# Revit family: GC-200-2000
name_source: partatom
category: Mechanical Equipment
units: mm (PartAtom-declared; Revit-internal decimal feet)

## family parameters
Always vertical = Yes
Cut with Voids When Loaded = No
Part Type = Normal
Room Calculation Point = No
Round Connector Dimension = Use Diameter
Shared = No
Work Plane-Based = No

## types (30) — shared parameters
0 = 0"
1" = 1"
1.5 = 1 1/2"
2" = 2"
2' = 24"
3" = 3"
4" = 4"
Manufacturer = Loren Cook Company
ONE EIGTH = 1/8"
Type Comments = Ceiling and Wall Blower 200-2000 Series
URL = www.lorencook.com

## per-type parameters (varying)
| type | (H/2)-(K/2) | A | A/2 | B | B/2 | H | H/2 | J | J/2 | K | K/2 | L | L/2 | Model | W | W/2 |
| GC-222/242_STEEL | -1 15/16" | 8" | 4" | 6" | 3" | 9 3/4" | 4 7/8" | 16 3/8" | 8 3/16" | 13 5/8" | 6 13/16" | 12 3/8" | 6 3/16" | GC | 9 3/4" | 4 7/8" |
| GC-322/342_STEEL | -1 7/16" | 8" | 4" | 6" | 3" | 10 3/4" | 5 3/8" | 16 3/8" | 8 3/16" | 13 5/8" | 6 13/16" | 12 3/8" | 6 3/16" | GC | 10 3/4" | 5 3/8" |
| GC-422_STEEL | -1 3/16" | 8" | 4" | 6" | 3" | 11 7/8" | 5 15/16" | 21" | 10 1/2" | 14 1/4" | 7 1/8" | 17" | 8 1/2" | GC | 11 7/8" | 5 15/16" |
| GC-520_STEEL | -1 3/16" | 8" | 4" | 6" | 3" | 11 7/8" | 5 15/16" | 21" | 10 1/2" | 14 1/4" | 7 1/8" | 17" | 8 1/2" | GC | 11 7/8" | 5 15/16" |
| GC-620/640_STEEL | -1 3/16" | 10 1/2" | 5 1/4" | 4 3/4" | 2 3/8" | 11 7/8" | 5 15/16" | 21" | 10 1/2" | 14 1/4" | 7 1/8" | 17" | 8 1/2" | GC | 11 7/8" | 5 15/16" |
| GC-720/740_STEEL | -1 3/16" | 10 1/2" | 5 1/4" | 4 3/4" | 2 3/8" | 11 7/8" | 5 15/16" | 21" | 10 1/2" | 14 1/4" | 7 1/8" | 17" | 8 1/2" | GC | 11 7/8" | 5 15/16" |
| GC-822/842/862_STEEL | -1 7/32" | 20" | 10" | 6" | 3" | 14 11/16" | 7 11/32" | 31 3/8" | 15 11/16" | 17 1/8" | 8 9/16" | 27" | 13 1/2" | GC | 14 11/16" | 7 11/32" |
| GC-920/940/960_STEEL | -1 7/32" | 24 1/4" | 12 1/8" | 6" | 3" | 14 11/16" | 7 11/32" | 35 1/8" | 17 9/16" | 17 1/8" | 8 9/16" | 31" | 15 1/2" | GC | 14 11/16" | 7 11/32" |
| GC-222/242_ALUMINUM | -3/4" | 8" | 4" | 6" | 3" | 9 3/4" | 4 7/8" | 14 1/4" | 7 1/8" | 11 1/4" | 5 5/8" | 12 3/8" | 6 3/16" | GC | 9 3/4" | 4 7/8" |
| GC-322/342_ALUMINUM | -3/4" | 8" | 4" | 6" | 3" | 10 3/4" | 5 3/8" | 14 1/4" | 7 1/8" | 12 1/4" | 6 1/8" | 12 3/8" | 6 3/16" | GC | 10 3/4" | 5 3/8" |
| GC-422_ALUMINUM | -15/16" | 8" | 4" | 6" | 3" | 11 7/8" | 5 15/16" | 18 3/4" | 9 3/8" | 13 3/4" | 6 7/8" | 17" | 8 1/2" | GC | 11 7/8" | 5 15/16" |
| GC-522/524_ALUMINUM | -15/16" | 8" | 4" | 6" | 3" | 11 7/8" | 5 15/16" | 18 3/4" | 9 3/8" | 13 3/4" | 6 7/8" | 17" | 8 1/2" | GC | 11 7/8" | 5 15/16" |
| GC-622/642_ALUMINUM | -15/16" | 10 1/2" | 5 1/4" | 4 3/4" | 2 3/8" | 11 7/8" | 5 15/16" | 18 3/4" | 9 3/8" | 13 3/4" | 6 7/8" | 17" | 8 1/2" | GC | 11 7/8" | 5 15/16" |
| GC-720/740_ALUMINUM | -15/16" | 10 1/2" | 5 1/4" | 4 3/4" | 2 3/8" | 11 7/8" | 5 15/16" | 18 3/4" | 9 3/8" | 13 3/4" | 6 7/8" | 17" | 8 1/2" | GC | 11 7/8" | 5 15/16" |
| GC-222/242_PLASTIC | -1 3/4" | 8" | 4" | 6" | 3" | 9 3/4" | 4 7/8" | 14 3/4" | 7 3/8" | 13 1/4" | 6 5/8" | 12 3/8" | 6 3/16" | GC | 9 3/4" | 4 7/8" |
| GC-822/842/862_ALUMINUM | -25/32" | 20" | 10" | 6" | 3" | 14 11/16" | 7 11/32" | 28 3/4" | 14 3/8" | 16 1/4" | 8 1/8" | 27" | 13 1/2" | GC | 14 11/16" | 7 11/32" |
| GC-920/940/960_ALUMINUM | -9/32" | 24 1/4" | 12 1/8" | 6" | 3" | 14 11/16" | 7 11/32" | 31 3/4" | 15 7/8" | 15 1/4" | 7 5/8" | 31" | 15 1/2" | GC | 14 11/16" | 7 11/32" |
| GC-1000_ALUMINUM | -1/4" | 33 11/16" | 16 27/32" | 7 11/16" | 3 27/32" | 15 1/4" | 7 5/8" | 38 3/4" | 19 3/8" | 15 3/4" | 7 7/8" | 38 1/8" | 19 1/16" | GC | 15 1/4" | 7 5/8" |
| GC-1000_STEEL | -15/16" | 33 11/16" | 16 27/32" | 7 11/16" | 3 27/32" | 15 1/4" | 7 5/8" | 42 3/8" | 21 3/16" | 17 1/8" | 8 9/16" | 38 1/8" | 19 1/16" | GC | 15 1/4" | 7 5/8" |
| GC-2000_ALUMINUM | -5/16" | 41 1/8" | 20 9/16" | 9 5/8" | 4 13/16" | 16 5/8" | 8 5/16" | 45 3/4" | 22 7/8" | 17 1/4" | 8 5/8" | 45 7/16" | 22 23/32" | GC | 16 5/8" | 8 5/16" |
| GC-2000_STEEL | -15/16" | 41 1/8" | 20 9/16" | 9 5/8" | 4 13/16" | 16 5/8" | 8 5/16" | 49 1/2" | 24 3/4" | 18 1/2" | 9 1/4" | 45 7/16" | 22 23/32" | GC | 16 5/8" | 8 5/16" |
| GC-322/342_PLASTIC | -1 1/4" | 8" | 4" | 6" | 3" | 10 3/4" | 5 3/8" | 14 3/4" | 7 3/8" | 13 1/4" | 6 5/8" | 12 3/8" | 6 3/16" | GC | 10 3/4" | 5 3/8" |
| GCVF-500_ALUMINUM | -15/16" | 8" | 4" | 6" | 3" | 11 7/8" | 5 15/16" | 18 3/4" | 9 3/8" | 13 3/4" | 6 7/8" | 17" | 8 1/2" | GC-VF | 11 7/8" | 5 15/16" |
| GCVF-500_STEEL | -1 3/16" | 8" | 4" | 6" | 3" | 11 7/8" | 5 15/16" | 21" | 10 1/2" | 14 1/4" | 7 1/8" | 17" | 8 1/2" | GC-VF | 11 7/8" | 5 15/16" |
| GCVF-700_ALUMINUM | -15/16" | 10 1/2" | 5 1/4" | 4 3/4" | 2 3/8" | 11 7/8" | 5 15/16" | 22 11/16" | 11 11/32" | 13 3/4" | 6 7/8" | 21" | 10 1/2" | GC-VF | 11 7/8" | 5 15/16" |
| GCVF-700_STEEL | -1 3/16" | 10 1/2" | 5 1/4" | 4 3/4" | 2 3/8" | 11 7/8" | 5 15/16" | 25" | 12 1/2" | 14 1/4" | 7 1/8" | 21" | 10 1/2" | GC-VF | 11 7/8" | 5 15/16" |
| GCVF-900_ALUMINUM | -25/32" | 24 1/4" | 12 1/8" | 6" | 3" | 14 11/16" | 7 11/32" | 32 3/4" | 16 3/8" | 16 1/4" | 8 1/8" | 31" | 15 1/2" | GC-VF | 14 11/16" | 7 11/32" |
| GCVF-900_STEEL | -1 7/32" | 24 1/4" | 12 1/8" | 6" | 3" | 14 11/16" | 7 11/32" | 35 1/8" | 17 9/16" | 17 1/8" | 8 9/16" | 31" | 15 1/2" | GC-VF | 14 11/16" | 7 11/32" |
| GCVF-300_ALUMINUM | -3/4" | 8" | 4" | 6" | 3" | 10 3/4" | 5 3/8" | 14 1/4" | 7 1/8" | 12 1/4" | 6 1/8" | 12 3/8" | 6 3/16" | GCVF | 10 3/4" | 5 3/8" |
| GCVF-340_STEEL | -3/4" | 8" | 4" | 6" | 3" | 10 3/4" | 5 3/8" | 14 1/4" | 7 1/8" | 12 1/4" | 6 1/8" | 12 3/8" | 6 3/16" | GCVF | 10 3/4" | 5 3/8" |
